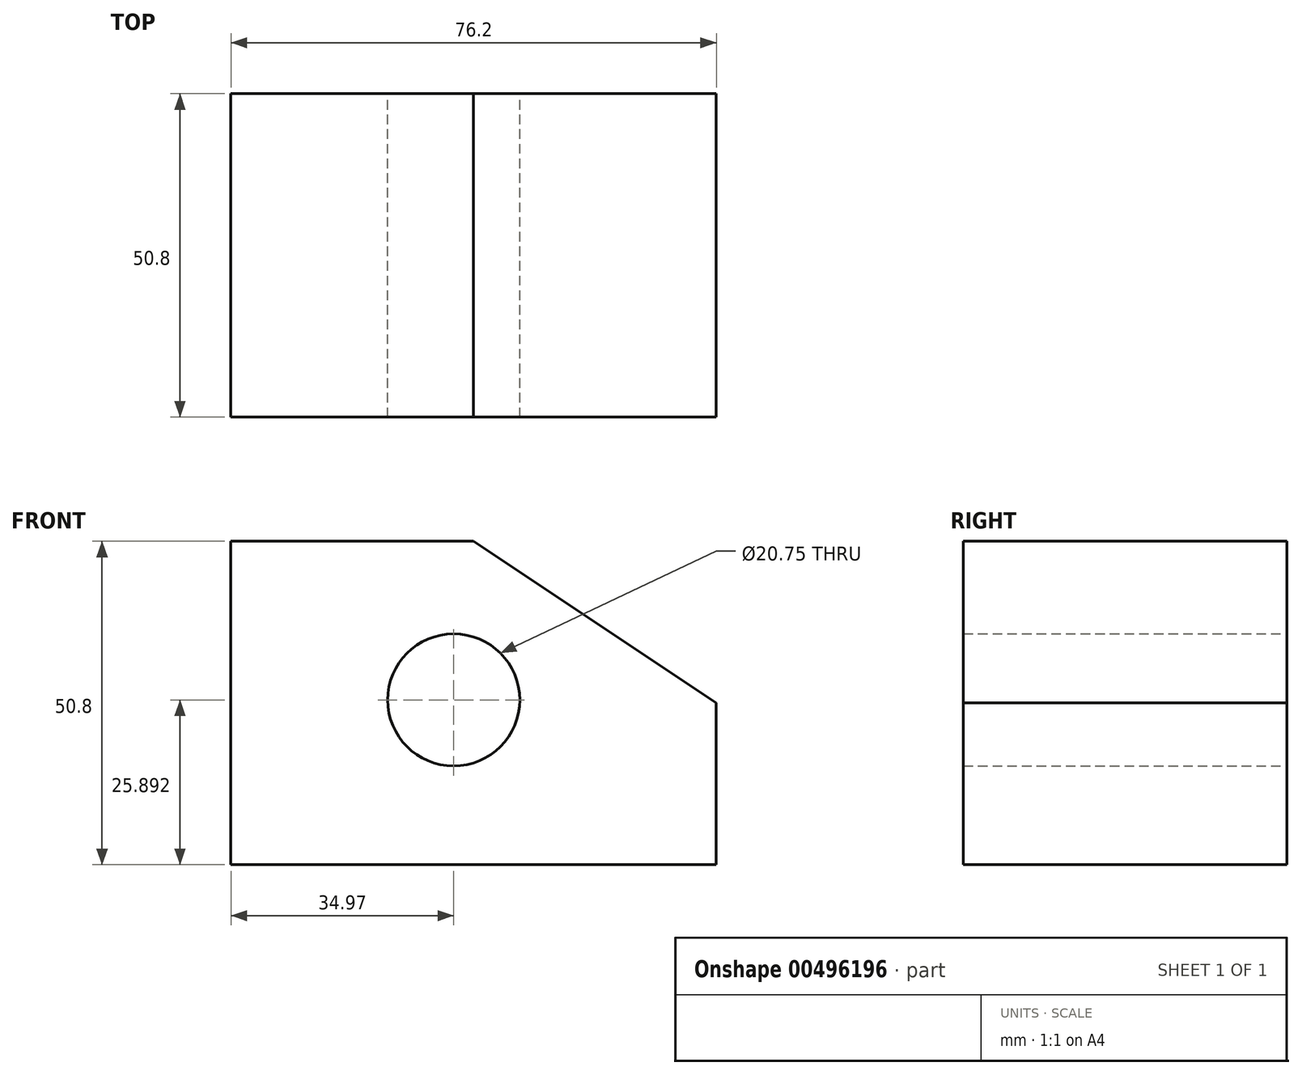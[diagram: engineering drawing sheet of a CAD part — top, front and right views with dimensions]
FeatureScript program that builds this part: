
annotation { "Feature Type Name" : "Feature", "Feature Type Description" : "" }
export const myFeature = defineFeature(function(context is Context, id is Id, definition is map)
    precondition{}
    {
        {
            var Q0;
            Q0=qCreatedBy(makeId("Front.planeOp"),FACE);
            var sketch = newSketch(context, id + "F0", { "sketchPlane" : qUnion([Q0])});
            skLineSegment(sketch, "E0.bottom", {"start": v(-31.16, 36.61) * mm, "end": v(6.94, 36.61) * mm});
            skLineSegment(sketch, "E0.top", {"start": v(-31.16, -14.19) * mm, "end": v(45.04, -14.19) * mm});
            skLineSegment(sketch, "E0.left", {"start": v(-31.16, 36.61) * mm, "end": v(-31.16, -14.19) * mm});
            skLineSegment(sketch, "E0.right", {"start": v(45.04, 11.21) * mm, "end": v(45.04, -14.19) * mm});
            skLineSegment(sketch, "E1", {"start": v(6.94, 36.61) * mm, "end": v(45.04, 11.21) * mm});
            skPoint(sketch, "E2.orphan", {"position": v(45.04, 36.61) * mm});
            skCircle(sketch, "E3", {"center": v(3.8, 11.7) * mm, "radius": 10.37 * mm});
            skSolve(sketch);
        }
        {
            var Q0;
            Q0=makeQuery(id+"F0.imprint","IMPRINT",FACE,{"disambiguationData":[TD([[makeQuery(id+"F0.imprint","IMPRINT",EDGE,{"derivedFrom":sQuery(id+"F0.wireOp",EDGE,"E0.bottom")}),-1.0]])]});
            extrude(context, id + "F1", {"entities" : qUnion([Q0]), "depth" : 50.8 * mm});
        }
    });
